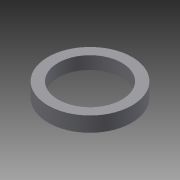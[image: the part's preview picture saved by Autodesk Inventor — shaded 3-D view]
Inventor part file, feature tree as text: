
AUTODESK INVENTOR PART (.ipt)
format: ipt  version: 2015 (Build 190159000, 159)  size: 104,448 bytes
history: native  units: in
note: dims shown in document units (in); Inventor stores cm internally (conversion verified against a paired STEP export)
features: revolve x1, sketch x1
ambient origin geometry x8: Origin, YZ Plane, XZ Plane, XY Plane, X Axis, Y Axis, Z Axis, Center Point
bodies: Solid1 (feature_tree)
feature tree (2):
  revolve  "Revolution1"  [1 undecoded]
  sketch  "Sketch1"  dims[d0=2.2in d1=1.75in d2=2.5in d3=0.0625in d4=90.0deg d5=0.125in d6=0.0625in d7=2.5in d8=1.5in d9=90.0deg d10=5.5in d11=90.0deg]
note: 1 required parameter value undecoded (feature->parameter linkage not recoverable at this tier; creation-order binding heuristic only, values carry confidence <= 0.55)
